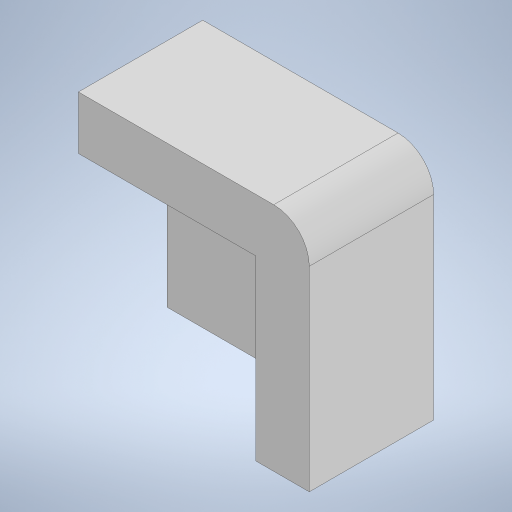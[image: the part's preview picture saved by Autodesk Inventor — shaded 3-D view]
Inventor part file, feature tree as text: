
AUTODESK INVENTOR PART (.ipt)
format: ipt  version: 2023 (Build 270158000, 158)  size: 210,432 bytes
history: native  units: mm
features: extrude x2, sketch x2, fillet x1
ambient origin geometry x8: Origin, YZ Plane, XZ Plane, XY Plane, X Axis, Y Axis, Z Axis, Center Point
bodies: Solide1 (feature_tree)
feature tree (5):
  extrude  "Extrusion1"  Depth=10.0mm
  extrude  "Extrusion2"  Depth=10.0mm
  fillet  "Congé1"  Radius=3.0mm
  sketch  "Esquisse1"
  sketch  "Esquisse2"
